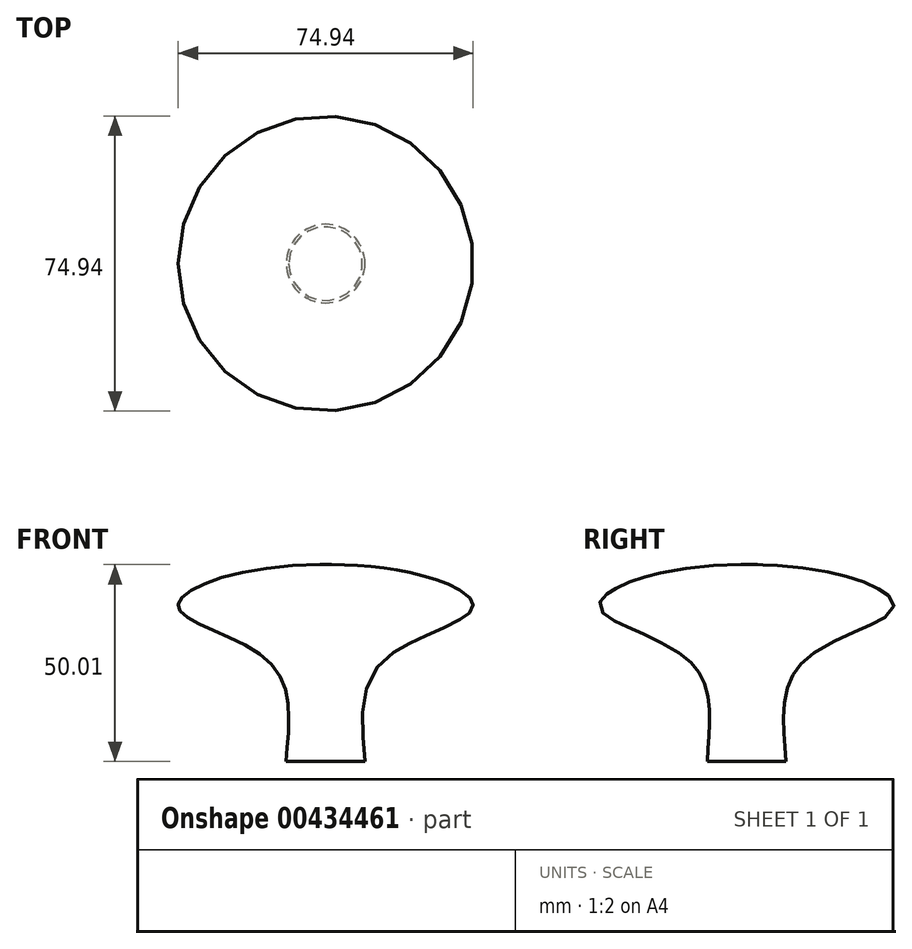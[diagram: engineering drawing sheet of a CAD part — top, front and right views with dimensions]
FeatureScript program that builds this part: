
annotation { "Feature Type Name" : "Feature", "Feature Type Description" : "" }
export const myFeature = defineFeature(function(context is Context, id is Id, definition is map)
    precondition{}
    {
        {
            var Q0;
            Q0=qCreatedBy(makeId("Front.planeOp"),FACE);
            var sketch = newSketch(context, id + "F0", { "sketchPlane" : qUnion([Q0])});
            skLineSegment(sketch, "E0", {"start": v(0, 0) * mm, "end": v(0, 50) * mm});
            skLineSegment(sketch, "E1", {"start": v(0, 0) * mm, "end": v(-10, 0) * mm});
            skFitSpline(sketch, "E2", {"points": [v(-10, 0) * mm, v(-13.81, 24.77) * mm, v(-37.34, 38.89) * mm, v(0, 50) * mm], "startDerivative": vector(4.29, 79.35) * mm, "endDerivative": vector(167.91, -2.42) * mm});
            skSolve(sketch);
        }
        {
            var Q0;
            Q0=makeQuery(id+"F0.imprint","IMPRINT",FACE,{"disambiguationData":[TD([[makeQuery(id+"F0.imprint","IMPRINT",EDGE,{"derivedFrom":sQuery(id+"F0.wireOp",EDGE,"E0")}),1.0]])]});
            var Q1;
            Q1=sQuery(id+"F0.wireOp",EDGE,"E0");
            revolve(context, id + "F1", {"entities" : qUnion([Q0]), "axis" : qUnion([Q1]), "revolveType" : RevolveType.FULL});
        }
    });
